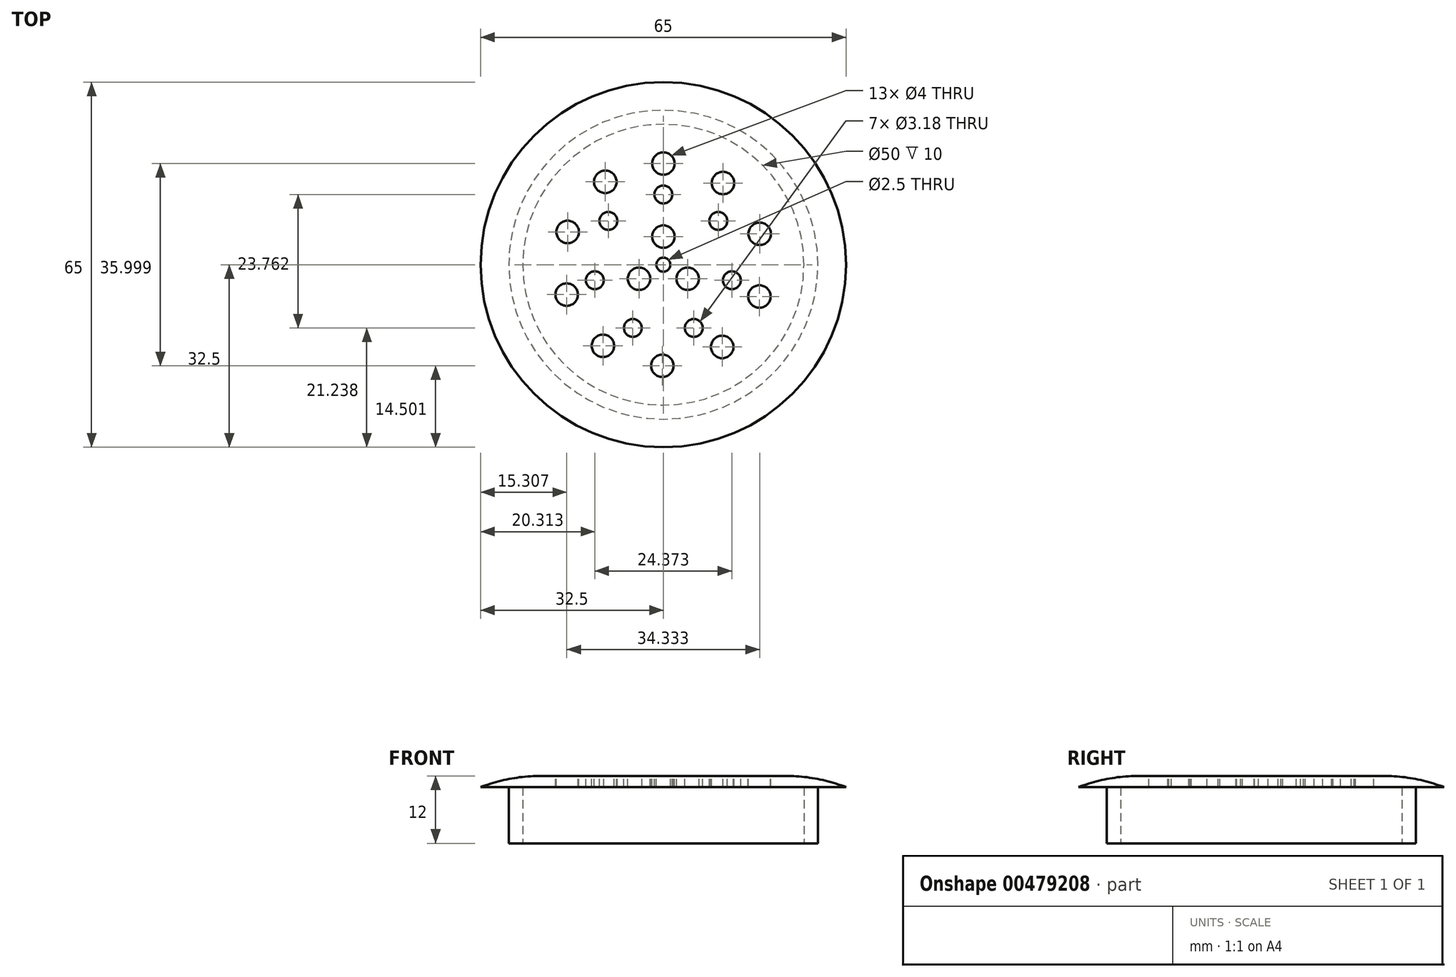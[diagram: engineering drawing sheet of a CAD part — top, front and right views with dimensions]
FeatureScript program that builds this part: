
annotation { "Feature Type Name" : "Feature", "Feature Type Description" : "" }
export const myFeature = defineFeature(function(context is Context, id is Id, definition is map)
    precondition{}
    {
        {
            var Q0;
            Q0=qCreatedBy(makeId("Top.planeOp"),FACE);
            var sketch = newSketch(context, id + "F0", { "sketchPlane" : qUnion([Q0])});
            skCircle(sketch, "E0", {"center": v(0, 0) * mm, "radius": 27.5 * mm});
            skCircle(sketch, "E1", {"center": v(0, 0) * mm, "radius": 25 * mm});
            skSolve(sketch);
        }
        {
            var Q0;
            Q0 = qSketchRegion(id + "F0", true);
            extrude(context, id + "F1", {"entities" : qUnion([Q0]), "depth" : 10 * mm, "offsetDistance" : 25 * mm});
        }
        {
            var Q0;
            Q0=makeQuery(id+"F1.opExtrude","CAP_FACE",FACE,{"disambiguationData":[OSD([sQuery(id+"F0.wireOp",EDGE,"E0"),sQuery(id+"F0.wireOp",EDGE,"E1")])],"isStart":false});
            var sketch = newSketch(context, id + "F2", { "sketchPlane" : qUnion([Q0])});
            skCircle(sketch, "E2", {"center": v(0, 0) * mm, "radius": 32.5 * mm});
            skSolve(sketch);
        }
        {
            var Q0;
            Q0 = qSketchRegion(id + "F2", true);
            extrude(context, id + "F3", {"entities" : qUnion([Q0]), "operationType" : NewBodyOperationType.ADD, "depth" : 2 * mm, "offsetDistance" : 25 * mm});
        }
        {
            var Q0;
            Q0=makeQuery(id+"F3.opExtrude","CAP_EDGE",EDGE,{"disambiguationData":[OSD([sQuery(id+"F2.wireOp",EDGE,"E2")])],"isStart":false});
            fillet(context, id + "F4", {"entities" : qUnion([Q0]), "radius" : 30 * mm, "tangentPropagation" : true, "allowEdgeOverflow" : false});
        }
        {
            var Q0;
            Q0=makeQuery(id+"F3.opExtrude","CAP_FACE",FACE,{"disambiguationData":[OSD([sQuery(id+"F2.wireOp",EDGE,"E2")])],"isStart":false});
            var sketch = newSketch(context, id + "F5", { "sketchPlane" : qUnion([Q0])});
            skCircle(sketch, "E3", {"center": v(0, 0) * mm, "radius": 1.25 * mm});
            skCircle(sketch, "E4", {"center": v(0, 0) * mm, "radius": 18 * mm});
            skCircle(sketch, "E5", {"center": v(0, 0) * mm, "radius": 12.5 * mm});
            skCircle(sketch, "E6", {"center": v(0, 0) * mm, "radius": 5 * mm});
            skCircle(sketch, "E7", {"center": v(0, 18) * mm, "radius": 2 * mm});
            skCircle(sketch, "E8", {"center": v(0, 5) * mm, "radius": 2 * mm});
            skCircle(sketch, "E9.1.0", {"center": v(10.6, 14.54) * mm, "radius": 2 * mm});
            skCircle(sketch, "E9.2.0", {"center": v(17.14, 5.5) * mm, "radius": 2 * mm});
            skCircle(sketch, "E9.3.0", {"center": v(17.09, -5.66) * mm, "radius": 2 * mm});
            skCircle(sketch, "E9.4.0", {"center": v(10.47, -14.64) * mm, "radius": 2 * mm});
            skCircle(sketch, "E9.5.0", {"center": v(-0.17, -18) * mm, "radius": 2 * mm});
            skCircle(sketch, "E9.6.0", {"center": v(-10.75, -14.44) * mm, "radius": 2 * mm});
            skCircle(sketch, "E9.7.0", {"center": v(-17.2, -5.33) * mm, "radius": 2 * mm});
            skCircle(sketch, "E9.8.0", {"center": v(-17.03, 5.83) * mm, "radius": 2 * mm});
            skCircle(sketch, "E9.9.0", {"center": v(-10.32, 14.74) * mm, "radius": 2 * mm});
            skLineSegment(sketch, "E9.anchor1", {"start": v(0, 0) * mm, "end": v(0, 18) * mm, "construction": true});
            skLineSegment(sketch, "E9.anchor2", {"start": v(0, 0) * mm, "end": v(-10.32, 14.74) * mm, "construction": true});
            skCircle(sketch, "E10", {"center": v(0, 12.5) * mm, "radius": 1.6 * mm});
            skCircle(sketch, "E11.1.0", {"center": v(-9.77, 7.8) * mm, "radius": 1.6 * mm});
            skCircle(sketch, "E11.2.0", {"center": v(-12.19, -2.78) * mm, "radius": 1.6 * mm});
            skCircle(sketch, "E11.3.0", {"center": v(-5.42, -11.26) * mm, "radius": 1.6 * mm});
            skCircle(sketch, "E11.4.0", {"center": v(5.42, -11.26) * mm, "radius": 1.6 * mm});
            skCircle(sketch, "E11.5.0", {"center": v(12.19, -2.78) * mm, "radius": 1.6 * mm});
            skCircle(sketch, "E11.6.0", {"center": v(9.77, 7.8) * mm, "radius": 1.6 * mm});
            skCircle(sketch, "E12.1.0", {"center": v(-4.33, -2.5) * mm, "radius": 2 * mm});
            skCircle(sketch, "E12.2.0", {"center": v(4.33, -2.5) * mm, "radius": 2 * mm});
            skSolve(sketch);
        }
        {
            var Q0;
            {var subQ0=sQuery(id+"F5.wireOp",EDGE,"E9.2.0");var subQ1=sQuery(id+"F5.wireOp",EDGE,"E4");var subQ2=makeQuery(id+"F5.imprint","INTERSECT",VERTEX,{"disambiguationData":[OD(0.0)],"derivedFrom":[subQ1,subQ0]});Q0=makeQuery(id+"F5.imprint","IMPRINT",FACE,{"disambiguationData":[TD([[makeQuery(id+"F5.imprint","IMPRINT",EDGE,{"disambiguationData":[TD([[subQ2,1.0]])],"derivedFrom":subQ1}),1.0]])]});}
            var Q1;
            {var subQ0=sQuery(id+"F5.wireOp",EDGE,"E9.2.0");var subQ1=sQuery(id+"F5.wireOp",EDGE,"E4");var subQ2=makeQuery(id+"F5.imprint","INTERSECT",VERTEX,{"disambiguationData":[OD(0.0)],"derivedFrom":[subQ1,subQ0]});Q1=makeQuery(id+"F5.imprint","IMPRINT",FACE,{"disambiguationData":[TD([[makeQuery(id+"F5.imprint","IMPRINT",EDGE,{"disambiguationData":[TD([[subQ2,1.0]])],"derivedFrom":subQ1}),-1.0]])]});}
            var Q2;
            {var subQ0=sQuery(id+"F5.wireOp",EDGE,"E9.1.0");var subQ1=sQuery(id+"F5.wireOp",EDGE,"E4");var subQ2=makeQuery(id+"F5.imprint","INTERSECT",VERTEX,{"disambiguationData":[OD(0.0)],"derivedFrom":[subQ1,subQ0]});Q2=makeQuery(id+"F5.imprint","IMPRINT",FACE,{"disambiguationData":[TD([[makeQuery(id+"F5.imprint","IMPRINT",EDGE,{"disambiguationData":[TD([[subQ2,-1.0]])],"derivedFrom":subQ1}),1.0]])]});}
            var Q3;
            {var subQ0=sQuery(id+"F5.wireOp",EDGE,"E9.1.0");var subQ1=sQuery(id+"F5.wireOp",EDGE,"E4");var subQ2=makeQuery(id+"F5.imprint","INTERSECT",VERTEX,{"disambiguationData":[OD(0.0)],"derivedFrom":[subQ1,subQ0]});Q3=makeQuery(id+"F5.imprint","IMPRINT",FACE,{"disambiguationData":[TD([[makeQuery(id+"F5.imprint","IMPRINT",EDGE,{"disambiguationData":[TD([[subQ2,-1.0]])],"derivedFrom":subQ1}),-1.0]])]});}
            var Q4;
            {var subQ0=sQuery(id+"F5.wireOp",EDGE,"E7");var subQ1=sQuery(id+"F5.wireOp",EDGE,"E4");var subQ2=makeQuery(id+"F5.imprint","INTERSECT",VERTEX,{"disambiguationData":[OD(0.0)],"derivedFrom":[subQ1,subQ0]});Q4=makeQuery(id+"F5.imprint","IMPRINT",FACE,{"disambiguationData":[TD([[makeQuery(id+"F5.imprint","IMPRINT",EDGE,{"disambiguationData":[TD([[subQ2,-1.0]])],"derivedFrom":subQ1}),1.0]])]});}
            var Q5;
            {var subQ0=sQuery(id+"F5.wireOp",EDGE,"E7");var subQ1=sQuery(id+"F5.wireOp",EDGE,"E4");var subQ2=makeQuery(id+"F5.imprint","INTERSECT",VERTEX,{"disambiguationData":[OD(0.0)],"derivedFrom":[subQ1,subQ0]});Q5=makeQuery(id+"F5.imprint","IMPRINT",FACE,{"disambiguationData":[TD([[makeQuery(id+"F5.imprint","IMPRINT",EDGE,{"disambiguationData":[TD([[subQ2,-1.0]])],"derivedFrom":subQ1}),-1.0]])]});}
            var Q6;
            {var subQ0=sQuery(id+"F5.wireOp",EDGE,"E9.9.0");var subQ1=sQuery(id+"F5.wireOp",EDGE,"E4");var subQ2=makeQuery(id+"F5.imprint","INTERSECT",VERTEX,{"disambiguationData":[OD(0.0)],"derivedFrom":[subQ1,subQ0]});Q6=makeQuery(id+"F5.imprint","IMPRINT",FACE,{"disambiguationData":[TD([[makeQuery(id+"F5.imprint","IMPRINT",EDGE,{"disambiguationData":[TD([[subQ2,-1.0]])],"derivedFrom":subQ1}),1.0]])]});}
            var Q7;
            {var subQ0=sQuery(id+"F5.wireOp",EDGE,"E9.9.0");var subQ1=sQuery(id+"F5.wireOp",EDGE,"E4");var subQ2=makeQuery(id+"F5.imprint","INTERSECT",VERTEX,{"disambiguationData":[OD(0.0)],"derivedFrom":[subQ1,subQ0]});Q7=makeQuery(id+"F5.imprint","IMPRINT",FACE,{"disambiguationData":[TD([[makeQuery(id+"F5.imprint","IMPRINT",EDGE,{"disambiguationData":[TD([[subQ2,-1.0]])],"derivedFrom":subQ1}),-1.0]])]});}
            var Q8;
            {var subQ0=sQuery(id+"F5.wireOp",EDGE,"E9.8.0");var subQ1=sQuery(id+"F5.wireOp",EDGE,"E4");var subQ2=makeQuery(id+"F5.imprint","INTERSECT",VERTEX,{"disambiguationData":[OD(0.0)],"derivedFrom":[subQ1,subQ0]});Q8=makeQuery(id+"F5.imprint","IMPRINT",FACE,{"disambiguationData":[TD([[makeQuery(id+"F5.imprint","IMPRINT",EDGE,{"disambiguationData":[TD([[subQ2,-1.0]])],"derivedFrom":subQ1}),1.0]])]});}
            var Q9;
            {var subQ0=sQuery(id+"F5.wireOp",EDGE,"E9.8.0");var subQ1=sQuery(id+"F5.wireOp",EDGE,"E4");var subQ2=makeQuery(id+"F5.imprint","INTERSECT",VERTEX,{"disambiguationData":[OD(0.0)],"derivedFrom":[subQ1,subQ0]});Q9=makeQuery(id+"F5.imprint","IMPRINT",FACE,{"disambiguationData":[TD([[makeQuery(id+"F5.imprint","IMPRINT",EDGE,{"disambiguationData":[TD([[subQ2,-1.0]])],"derivedFrom":subQ1}),-1.0]])]});}
            var Q10;
            {var subQ0=sQuery(id+"F5.wireOp",EDGE,"E9.7.0");var subQ1=sQuery(id+"F5.wireOp",EDGE,"E4");var subQ2=makeQuery(id+"F5.imprint","INTERSECT",VERTEX,{"disambiguationData":[OD(0.0)],"derivedFrom":[subQ1,subQ0]});Q10=makeQuery(id+"F5.imprint","IMPRINT",FACE,{"disambiguationData":[TD([[makeQuery(id+"F5.imprint","IMPRINT",EDGE,{"disambiguationData":[TD([[subQ2,-1.0]])],"derivedFrom":subQ1}),1.0]])]});}
            var Q11;
            {var subQ0=sQuery(id+"F5.wireOp",EDGE,"E9.7.0");var subQ1=sQuery(id+"F5.wireOp",EDGE,"E4");var subQ2=makeQuery(id+"F5.imprint","INTERSECT",VERTEX,{"disambiguationData":[OD(0.0)],"derivedFrom":[subQ1,subQ0]});Q11=makeQuery(id+"F5.imprint","IMPRINT",FACE,{"disambiguationData":[TD([[makeQuery(id+"F5.imprint","IMPRINT",EDGE,{"disambiguationData":[TD([[subQ2,-1.0]])],"derivedFrom":subQ1}),-1.0]])]});}
            var Q12;
            {var subQ0=sQuery(id+"F5.wireOp",EDGE,"E9.6.0");var subQ1=sQuery(id+"F5.wireOp",EDGE,"E4");var subQ2=makeQuery(id+"F5.imprint","INTERSECT",VERTEX,{"disambiguationData":[OD(0.0)],"derivedFrom":[subQ1,subQ0]});Q12=makeQuery(id+"F5.imprint","IMPRINT",FACE,{"disambiguationData":[TD([[makeQuery(id+"F5.imprint","IMPRINT",EDGE,{"disambiguationData":[TD([[subQ2,-1.0]])],"derivedFrom":subQ1}),1.0]])]});}
            var Q13;
            {var subQ0=sQuery(id+"F5.wireOp",EDGE,"E9.6.0");var subQ1=sQuery(id+"F5.wireOp",EDGE,"E4");var subQ2=makeQuery(id+"F5.imprint","INTERSECT",VERTEX,{"disambiguationData":[OD(0.0)],"derivedFrom":[subQ1,subQ0]});Q13=makeQuery(id+"F5.imprint","IMPRINT",FACE,{"disambiguationData":[TD([[makeQuery(id+"F5.imprint","IMPRINT",EDGE,{"disambiguationData":[TD([[subQ2,-1.0]])],"derivedFrom":subQ1}),-1.0]])]});}
            var Q14;
            {var subQ0=sQuery(id+"F5.wireOp",EDGE,"E9.5.0");var subQ1=sQuery(id+"F5.wireOp",EDGE,"E4");var subQ2=makeQuery(id+"F5.imprint","INTERSECT",VERTEX,{"disambiguationData":[OD(0.0)],"derivedFrom":[subQ1,subQ0]});Q14=makeQuery(id+"F5.imprint","IMPRINT",FACE,{"disambiguationData":[TD([[makeQuery(id+"F5.imprint","IMPRINT",EDGE,{"disambiguationData":[TD([[subQ2,-1.0]])],"derivedFrom":subQ1}),1.0]])]});}
            var Q15;
            {var subQ0=sQuery(id+"F5.wireOp",EDGE,"E9.5.0");var subQ1=sQuery(id+"F5.wireOp",EDGE,"E4");var subQ2=makeQuery(id+"F5.imprint","INTERSECT",VERTEX,{"disambiguationData":[OD(0.0)],"derivedFrom":[subQ1,subQ0]});Q15=makeQuery(id+"F5.imprint","IMPRINT",FACE,{"disambiguationData":[TD([[makeQuery(id+"F5.imprint","IMPRINT",EDGE,{"disambiguationData":[TD([[subQ2,-1.0]])],"derivedFrom":subQ1}),-1.0]])]});}
            var Q16;
            {var subQ0=sQuery(id+"F5.wireOp",EDGE,"E9.4.0");var subQ1=sQuery(id+"F5.wireOp",EDGE,"E4");var subQ2=makeQuery(id+"F5.imprint","INTERSECT",VERTEX,{"disambiguationData":[OD(0.0)],"derivedFrom":[subQ1,subQ0]});Q16=makeQuery(id+"F5.imprint","IMPRINT",FACE,{"disambiguationData":[TD([[makeQuery(id+"F5.imprint","IMPRINT",EDGE,{"disambiguationData":[TD([[subQ2,-1.0]])],"derivedFrom":subQ1}),1.0]])]});}
            var Q17;
            {var subQ0=sQuery(id+"F5.wireOp",EDGE,"E9.4.0");var subQ1=sQuery(id+"F5.wireOp",EDGE,"E4");var subQ2=makeQuery(id+"F5.imprint","INTERSECT",VERTEX,{"disambiguationData":[OD(0.0)],"derivedFrom":[subQ1,subQ0]});Q17=makeQuery(id+"F5.imprint","IMPRINT",FACE,{"disambiguationData":[TD([[makeQuery(id+"F5.imprint","IMPRINT",EDGE,{"disambiguationData":[TD([[subQ2,-1.0]])],"derivedFrom":subQ1}),-1.0]])]});}
            var Q18;
            {var subQ0=sQuery(id+"F5.wireOp",EDGE,"E9.3.0");var subQ1=sQuery(id+"F5.wireOp",EDGE,"E4");var subQ2=makeQuery(id+"F5.imprint","INTERSECT",VERTEX,{"disambiguationData":[OD(0.0)],"derivedFrom":[subQ1,subQ0]});Q18=makeQuery(id+"F5.imprint","IMPRINT",FACE,{"disambiguationData":[TD([[makeQuery(id+"F5.imprint","IMPRINT",EDGE,{"disambiguationData":[TD([[subQ2,-1.0]])],"derivedFrom":subQ1}),1.0]])]});}
            var Q19;
            {var subQ0=sQuery(id+"F5.wireOp",EDGE,"E9.3.0");var subQ1=sQuery(id+"F5.wireOp",EDGE,"E4");var subQ2=makeQuery(id+"F5.imprint","INTERSECT",VERTEX,{"disambiguationData":[OD(0.0)],"derivedFrom":[subQ1,subQ0]});Q19=makeQuery(id+"F5.imprint","IMPRINT",FACE,{"disambiguationData":[TD([[makeQuery(id+"F5.imprint","IMPRINT",EDGE,{"disambiguationData":[TD([[subQ2,-1.0]])],"derivedFrom":subQ1}),-1.0]])]});}
            var Q20;
            {var subQ0=sQuery(id+"F5.wireOp",EDGE,"E11.2.0");var subQ1=sQuery(id+"F5.wireOp",EDGE,"E5");var subQ2=makeQuery(id+"F5.imprint","INTERSECT",VERTEX,{"disambiguationData":[OD(0.0)],"derivedFrom":[subQ1,subQ0]});Q20=makeQuery(id+"F5.imprint","IMPRINT",FACE,{"disambiguationData":[TD([[makeQuery(id+"F5.imprint","IMPRINT",EDGE,{"disambiguationData":[TD([[subQ2,-1.0]])],"derivedFrom":subQ1}),-1.0]])]});}
            var Q21;
            {var subQ0=sQuery(id+"F5.wireOp",EDGE,"E11.2.0");var subQ1=sQuery(id+"F5.wireOp",EDGE,"E5");var subQ2=makeQuery(id+"F5.imprint","INTERSECT",VERTEX,{"disambiguationData":[OD(0.0)],"derivedFrom":[subQ1,subQ0]});Q21=makeQuery(id+"F5.imprint","IMPRINT",FACE,{"disambiguationData":[TD([[makeQuery(id+"F5.imprint","IMPRINT",EDGE,{"disambiguationData":[TD([[subQ2,-1.0]])],"derivedFrom":subQ1}),1.0]])]});}
            var Q22;
            {var subQ0=sQuery(id+"F5.wireOp",EDGE,"E11.1.0");var subQ1=sQuery(id+"F5.wireOp",EDGE,"E5");var subQ2=makeQuery(id+"F5.imprint","INTERSECT",VERTEX,{"disambiguationData":[OD(0.0)],"derivedFrom":[subQ1,subQ0]});Q22=makeQuery(id+"F5.imprint","IMPRINT",FACE,{"disambiguationData":[TD([[makeQuery(id+"F5.imprint","IMPRINT",EDGE,{"disambiguationData":[TD([[subQ2,-1.0]])],"derivedFrom":subQ1}),-1.0]])]});}
            var Q23;
            {var subQ0=sQuery(id+"F5.wireOp",EDGE,"E11.1.0");var subQ1=sQuery(id+"F5.wireOp",EDGE,"E5");var subQ2=makeQuery(id+"F5.imprint","INTERSECT",VERTEX,{"disambiguationData":[OD(0.0)],"derivedFrom":[subQ1,subQ0]});Q23=makeQuery(id+"F5.imprint","IMPRINT",FACE,{"disambiguationData":[TD([[makeQuery(id+"F5.imprint","IMPRINT",EDGE,{"disambiguationData":[TD([[subQ2,-1.0]])],"derivedFrom":subQ1}),1.0]])]});}
            var Q24;
            {var subQ0=sQuery(id+"F5.wireOp",EDGE,"E10");var subQ1=sQuery(id+"F5.wireOp",EDGE,"E5");var subQ2=makeQuery(id+"F5.imprint","INTERSECT",VERTEX,{"disambiguationData":[OD(0.0)],"derivedFrom":[subQ1,subQ0]});Q24=makeQuery(id+"F5.imprint","IMPRINT",FACE,{"disambiguationData":[TD([[makeQuery(id+"F5.imprint","IMPRINT",EDGE,{"disambiguationData":[TD([[subQ2,-1.0]])],"derivedFrom":subQ1}),1.0]])]});}
            var Q25;
            {var subQ0=sQuery(id+"F5.wireOp",EDGE,"E10");var subQ1=sQuery(id+"F5.wireOp",EDGE,"E5");var subQ2=makeQuery(id+"F5.imprint","INTERSECT",VERTEX,{"disambiguationData":[OD(0.0)],"derivedFrom":[subQ1,subQ0]});Q25=makeQuery(id+"F5.imprint","IMPRINT",FACE,{"disambiguationData":[TD([[makeQuery(id+"F5.imprint","IMPRINT",EDGE,{"disambiguationData":[TD([[subQ2,-1.0]])],"derivedFrom":subQ1}),-1.0]])]});}
            var Q26;
            {var subQ0=sQuery(id+"F5.wireOp",EDGE,"E11.6.0");var subQ1=sQuery(id+"F5.wireOp",EDGE,"E5");var subQ2=makeQuery(id+"F5.imprint","INTERSECT",VERTEX,{"disambiguationData":[OD(0.0)],"derivedFrom":[subQ1,subQ0]});Q26=makeQuery(id+"F5.imprint","IMPRINT",FACE,{"disambiguationData":[TD([[makeQuery(id+"F5.imprint","IMPRINT",EDGE,{"disambiguationData":[TD([[subQ2,1.0]])],"derivedFrom":subQ1}),-1.0]])]});}
            var Q27;
            {var subQ0=sQuery(id+"F5.wireOp",EDGE,"E11.6.0");var subQ1=sQuery(id+"F5.wireOp",EDGE,"E5");var subQ2=makeQuery(id+"F5.imprint","INTERSECT",VERTEX,{"disambiguationData":[OD(0.0)],"derivedFrom":[subQ1,subQ0]});Q27=makeQuery(id+"F5.imprint","IMPRINT",FACE,{"disambiguationData":[TD([[makeQuery(id+"F5.imprint","IMPRINT",EDGE,{"disambiguationData":[TD([[subQ2,1.0]])],"derivedFrom":subQ1}),1.0]])]});}
            var Q28;
            {var subQ0=sQuery(id+"F5.wireOp",EDGE,"E11.5.0");var subQ1=sQuery(id+"F5.wireOp",EDGE,"E5");var subQ2=makeQuery(id+"F5.imprint","INTERSECT",VERTEX,{"disambiguationData":[OD(0.0)],"derivedFrom":[subQ1,subQ0]});Q28=makeQuery(id+"F5.imprint","IMPRINT",FACE,{"disambiguationData":[TD([[makeQuery(id+"F5.imprint","IMPRINT",EDGE,{"disambiguationData":[TD([[subQ2,-1.0]])],"derivedFrom":subQ1}),1.0]])]});}
            var Q29;
            {var subQ0=sQuery(id+"F5.wireOp",EDGE,"E11.5.0");var subQ1=sQuery(id+"F5.wireOp",EDGE,"E5");var subQ2=makeQuery(id+"F5.imprint","INTERSECT",VERTEX,{"disambiguationData":[OD(0.0)],"derivedFrom":[subQ1,subQ0]});Q29=makeQuery(id+"F5.imprint","IMPRINT",FACE,{"disambiguationData":[TD([[makeQuery(id+"F5.imprint","IMPRINT",EDGE,{"disambiguationData":[TD([[subQ2,-1.0]])],"derivedFrom":subQ1}),-1.0]])]});}
            var Q30;
            {var subQ0=sQuery(id+"F5.wireOp",EDGE,"E11.4.0");var subQ1=sQuery(id+"F5.wireOp",EDGE,"E5");var subQ2=makeQuery(id+"F5.imprint","INTERSECT",VERTEX,{"disambiguationData":[OD(0.0)],"derivedFrom":[subQ1,subQ0]});Q30=makeQuery(id+"F5.imprint","IMPRINT",FACE,{"disambiguationData":[TD([[makeQuery(id+"F5.imprint","IMPRINT",EDGE,{"disambiguationData":[TD([[subQ2,-1.0]])],"derivedFrom":subQ1}),-1.0]])]});}
            var Q31;
            {var subQ0=sQuery(id+"F5.wireOp",EDGE,"E11.4.0");var subQ1=sQuery(id+"F5.wireOp",EDGE,"E5");var subQ2=makeQuery(id+"F5.imprint","INTERSECT",VERTEX,{"disambiguationData":[OD(0.0)],"derivedFrom":[subQ1,subQ0]});Q31=makeQuery(id+"F5.imprint","IMPRINT",FACE,{"disambiguationData":[TD([[makeQuery(id+"F5.imprint","IMPRINT",EDGE,{"disambiguationData":[TD([[subQ2,-1.0]])],"derivedFrom":subQ1}),1.0]])]});}
            var Q32;
            {var subQ0=sQuery(id+"F5.wireOp",EDGE,"E11.3.0");var subQ1=sQuery(id+"F5.wireOp",EDGE,"E5");var subQ2=makeQuery(id+"F5.imprint","INTERSECT",VERTEX,{"disambiguationData":[OD(0.0)],"derivedFrom":[subQ1,subQ0]});Q32=makeQuery(id+"F5.imprint","IMPRINT",FACE,{"disambiguationData":[TD([[makeQuery(id+"F5.imprint","IMPRINT",EDGE,{"disambiguationData":[TD([[subQ2,-1.0]])],"derivedFrom":subQ1}),1.0]])]});}
            var Q33;
            {var subQ0=sQuery(id+"F5.wireOp",EDGE,"E11.3.0");var subQ1=sQuery(id+"F5.wireOp",EDGE,"E5");var subQ2=makeQuery(id+"F5.imprint","INTERSECT",VERTEX,{"disambiguationData":[OD(0.0)],"derivedFrom":[subQ1,subQ0]});Q33=makeQuery(id+"F5.imprint","IMPRINT",FACE,{"disambiguationData":[TD([[makeQuery(id+"F5.imprint","IMPRINT",EDGE,{"disambiguationData":[TD([[subQ2,-1.0]])],"derivedFrom":subQ1}),-1.0]])]});}
            var Q34;
            {var subQ0=sQuery(id+"F5.wireOp",EDGE,"E12.1.0");var subQ1=sQuery(id+"F5.wireOp",EDGE,"E6");var subQ2=makeQuery(id+"F5.imprint","INTERSECT",VERTEX,{"disambiguationData":[OD(0.0)],"derivedFrom":[subQ1,subQ0]});Q34=makeQuery(id+"F5.imprint","IMPRINT",FACE,{"disambiguationData":[TD([[makeQuery(id+"F5.imprint","IMPRINT",EDGE,{"disambiguationData":[TD([[subQ2,-1.0]])],"derivedFrom":subQ1}),-1.0]])]});}
            var Q35;
            {var subQ0=sQuery(id+"F5.wireOp",EDGE,"E12.1.0");var subQ1=sQuery(id+"F5.wireOp",EDGE,"E6");var subQ2=makeQuery(id+"F5.imprint","INTERSECT",VERTEX,{"disambiguationData":[OD(0.0)],"derivedFrom":[subQ1,subQ0]});Q35=makeQuery(id+"F5.imprint","IMPRINT",FACE,{"disambiguationData":[TD([[makeQuery(id+"F5.imprint","IMPRINT",EDGE,{"disambiguationData":[TD([[subQ2,-1.0]])],"derivedFrom":subQ1}),1.0]])]});}
            var Q36;
            Q36=makeQuery(id+"F5.imprint","IMPRINT",FACE,{"disambiguationData":[TD([[makeQuery(id+"F5.imprint","IMPRINT",EDGE,{"derivedFrom":sQuery(id+"F5.wireOp",EDGE,"E3")}),1.0]])]});
            var Q37;
            {var subQ0=sQuery(id+"F5.wireOp",EDGE,"E6");var subQ1=sQuery(id+"F5.wireOp",EDGE,"E8");var subQ2=makeQuery(id+"F5.imprint","INTERSECT",VERTEX,{"disambiguationData":[OD(0.0)],"derivedFrom":[subQ1,subQ0]});Q37=makeQuery(id+"F5.imprint","IMPRINT",FACE,{"disambiguationData":[TD([[makeQuery(id+"F5.imprint","IMPRINT",EDGE,{"disambiguationData":[TD([[subQ2,1.0]])],"derivedFrom":subQ1}),1.0]])]});}
            var Q38;
            {var subQ0=sQuery(id+"F5.wireOp",EDGE,"E6");var subQ1=sQuery(id+"F5.wireOp",EDGE,"E8");var subQ2=makeQuery(id+"F5.imprint","INTERSECT",VERTEX,{"disambiguationData":[OD(0.0)],"derivedFrom":[subQ1,subQ0]});Q38=makeQuery(id+"F5.imprint","IMPRINT",FACE,{"disambiguationData":[TD([[makeQuery(id+"F5.imprint","IMPRINT",EDGE,{"disambiguationData":[TD([[subQ2,-1.0]])],"derivedFrom":subQ1}),1.0]])]});}
            var Q39;
            {var subQ0=sQuery(id+"F5.wireOp",EDGE,"E12.2.0");var subQ1=sQuery(id+"F5.wireOp",EDGE,"E6");var subQ2=makeQuery(id+"F5.imprint","INTERSECT",VERTEX,{"disambiguationData":[OD(0.0)],"derivedFrom":[subQ1,subQ0]});Q39=makeQuery(id+"F5.imprint","IMPRINT",FACE,{"disambiguationData":[TD([[makeQuery(id+"F5.imprint","IMPRINT",EDGE,{"disambiguationData":[TD([[subQ2,-1.0]])],"derivedFrom":subQ1}),1.0]])]});}
            var Q40;
            {var subQ0=sQuery(id+"F5.wireOp",EDGE,"E12.2.0");var subQ1=sQuery(id+"F5.wireOp",EDGE,"E6");var subQ2=makeQuery(id+"F5.imprint","INTERSECT",VERTEX,{"disambiguationData":[OD(0.0)],"derivedFrom":[subQ1,subQ0]});Q40=makeQuery(id+"F5.imprint","IMPRINT",FACE,{"disambiguationData":[TD([[makeQuery(id+"F5.imprint","IMPRINT",EDGE,{"disambiguationData":[TD([[subQ2,-1.0]])],"derivedFrom":subQ1}),-1.0]])]});}
            extrude(context, id + "F6", {"entities" : qUnion([Q0, Q1, Q2, Q3, Q4, Q5, Q6, Q7, Q8, Q9, Q10, Q11, Q12, Q13, Q14, Q15, Q16, Q17, Q18, Q19, Q20, Q21, Q22, Q23, Q24, Q25, Q26, Q27, Q28, Q29, Q30, Q31, Q32, Q33, Q34, Q35, Q36, Q37, Q38, Q39, Q40]), "operationType" : NewBodyOperationType.REMOVE, "oppositeDirection" : true, "depth" : 25 * mm, "offsetDistance" : 25 * mm});
        }
    });
